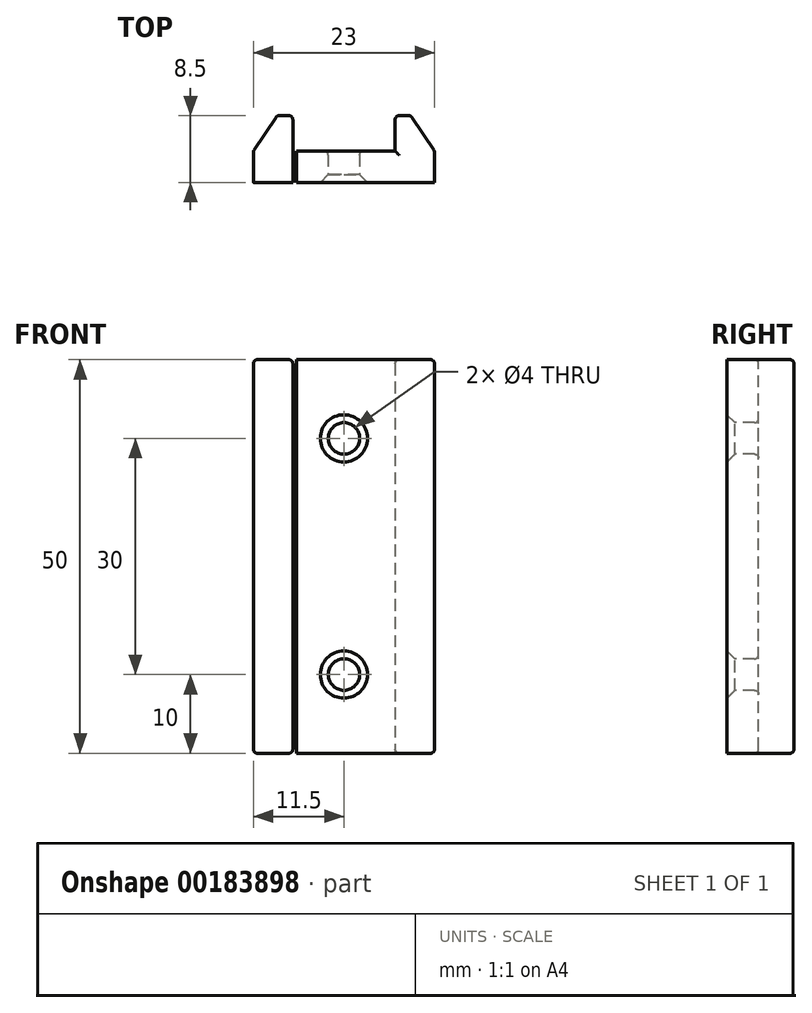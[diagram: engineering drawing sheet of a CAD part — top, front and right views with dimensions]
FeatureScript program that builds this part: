
annotation { "Feature Type Name" : "Feature", "Feature Type Description" : "" }
export const myFeature = defineFeature(function(context is Context, id is Id, definition is map)
    precondition{}
    {
        {
            var Q0;
            Q0=qCreatedBy(makeId("Front.planeOp"),FACE);
            var sketch = newSketch(context, id + "F0", { "sketchPlane" : qUnion([Q0])});
            skLineSegment(sketch, "E0.bottom", {"start": v(6, -25) * mm, "end": v(-6, -25) * mm});
            skLineSegment(sketch, "E0.top", {"start": v(6, 25) * mm, "end": v(-6, 25) * mm});
            skLineSegment(sketch, "E0.left", {"start": v(6, -25) * mm, "end": v(6, 25) * mm});
            skLineSegment(sketch, "E0.right", {"start": v(-6, -25) * mm, "end": v(-6, 25) * mm});
            skPoint(sketch, "E0.middle", {"position": v(0, 0) * mm});
            skLineSegment(sketch, "E1.bottom", {"start": v(-6, 25) * mm, "end": v(-11.5, 25) * mm});
            skLineSegment(sketch, "E1.top", {"start": v(-6, -25) * mm, "end": v(-11.5, -25) * mm});
            skLineSegment(sketch, "E1.left", {"start": v(-6, 25) * mm, "end": v(-6, -25) * mm});
            skLineSegment(sketch, "E1.right", {"start": v(-11.5, 25) * mm, "end": v(-11.5, -25) * mm});
            skLineSegment(sketch, "E2.MirrorCS", {"start": v(6.5, 25) * mm, "end": v(11.5, 25) * mm});
            skLineSegment(sketch, "E3.MirrorCS", {"start": v(11.5, 25) * mm, "end": v(11.5, -25) * mm});
            skLineSegment(sketch, "E4.MirrorCS", {"start": v(6.5, -25) * mm, "end": v(11.5, -25) * mm});
            skLineSegment(sketch, "E5.0", {"start": v(-6.5, 25) * mm, "end": v(-6.5, -25) * mm});
            skLineSegment(sketch, "E6.MirrorCS", {"start": v(6.5, 25) * mm, "end": v(6.5, -25) * mm});
            skLineSegment(sketch, "E7", {"start": v(0, 25) * mm, "end": v(0, -25) * mm, "construction": true});
            skLineSegment(sketch, "E8", {"start": v(-11.5, -15) * mm, "end": v(11.5, -15) * mm, "construction": true});
            skLineSegment(sketch, "E9", {"start": v(-11.5, 15) * mm, "end": v(11.5, 15) * mm, "construction": true});
            skCircle(sketch, "E10", {"center": v(0, 15) * mm, "radius": 2 * mm});
            skCircle(sketch, "E11", {"center": v(0, -15) * mm, "radius": 2 * mm});
            skLineSegment(sketch, "E12", {"start": v(6.5, 25) * mm, "end": v(6, 25) * mm});
            skLineSegment(sketch, "E13", {"start": v(6.5, -25) * mm, "end": v(6, -25) * mm});
            skSolve(sketch);
        }
        {
            var Q0;
            Q0=makeQuery(id+"F0.imprint","IMPRINT",FACE,{"disambiguationData":[TD([[makeQuery(id+"F0.imprint","IMPRINT",EDGE,{"derivedFrom":sQuery(id+"F0.wireOp",EDGE,"E0.bottom")}),-1.0]])]});
            var Q1;
            {var subQ1=sQuery(id+"F0.wireOp",EDGE,"E1.right");Q1=makeQuery(id+"F0.imprint","IMPRINT",FACE,{"disambiguationData":[TD([[makeQuery(id+"F0.imprint","IMPRINT",EDGE,{"derivedFrom":subQ1}),1.0]])]});}
            var Q2;
            {var subQ0=sQuery(id+"F0.wireOp",EDGE,"E1.left");Q2=makeQuery(id+"F0.imprint","IMPRINT",FACE,{"disambiguationData":[TD([[makeQuery(id+"F0.imprint","IMPRINT",EDGE,{"derivedFrom":subQ0}),-1.0]])]});}
            var Q3;
            Q3=makeQuery(id+"F0.imprint","IMPRINT",FACE,{"disambiguationData":[TD([[makeQuery(id+"F0.imprint","IMPRINT",EDGE,{"derivedFrom":sQuery(id+"F0.wireOp",EDGE,"E0.left")}),-1.0]])]});
            var Q4;
            Q4=makeQuery(id+"F0.imprint","IMPRINT",FACE,{"disambiguationData":[TD([[makeQuery(id+"F0.imprint","IMPRINT",EDGE,{"derivedFrom":sQuery(id+"F0.wireOp",EDGE,"E2.MirrorCS")}),-1.0]])]});
            extrude(context, id + "F1", {"entities" : qUnion([Q0, Q1, Q2, Q3, Q4]), "oppositeDirection" : true, "depth" : 4 * mm});
        }
        {
            var Q0;
            {var subQ0=sQuery(id+"F0.wireOp",EDGE,"E1.right");Q0=makeQuery(id+"F0.imprint","IMPRINT",FACE,{"disambiguationData":[TD([[makeQuery(id+"F0.imprint","IMPRINT",EDGE,{"derivedFrom":subQ0}),1.0]])]});}
            var Q1;
            {var subQ0=sQuery(id+"F0.wireOp",EDGE,"E3.MirrorCS");Q1=makeQuery(id+"F0.imprint","IMPRINT",FACE,{"disambiguationData":[TD([[makeQuery(id+"F0.imprint","IMPRINT",EDGE,{"derivedFrom":subQ0}),-1.0]])]});}
            extrude(context, id + "F2", {"entities" : qUnion([Q0, Q1]), "operationType" : NewBodyOperationType.ADD, "oppositeDirection" : true, "depth" : 8.5 * mm});
        }
        {
            var Q0;
            Q0=makeQuery(id+"F2.opExtrude","CAP_EDGE",EDGE,{"disambiguationData":[OSD([sQuery(id+"F0.wireOp",EDGE,"E1.right")])],"isStart":false});
            chamfer(context, id + "F3", {"entities" : qUnion([Q0]), "chamferType" : ChamferType.TWO_OFFSETS, "width1" : 4.5 * mm, "oppositeDirection" : false, "width2" : 3 * mm});
        }
        {
            var Q0;
            Q0=makeQuery(id+"F2.opExtrude","CAP_EDGE",EDGE,{"disambiguationData":[OSD([sQuery(id+"F0.wireOp",EDGE,"E3.MirrorCS")])],"isStart":false});
            chamfer(context, id + "F4", {"entities" : qUnion([Q0]), "chamferType" : ChamferType.TWO_OFFSETS, "width1" : 4.5 * mm, "oppositeDirection" : true, "width2" : 3 * mm, "tangentPropagation" : true});
        }
        {
            var Q0;
            Q0=sQuery(id+"F0.wireOp",VERTEX,"E10.center");
            var Q1;
            Q1=sQuery(id+"F0.wireOp",VERTEX,"E11.center");
            var Q2;
            Q2=makeQuery(id+"F1.opExtrude","SWEPT_BODY",BODY,{"disambiguationData":[OSD([sQuery(id+"F0.wireOp",EDGE,"E0.bottom"),sQuery(id+"F0.wireOp",EDGE,"E0.top"),sQuery(id+"F0.wireOp",EDGE,"E1.bottom"),sQuery(id+"F0.wireOp",EDGE,"E1.top"),sQuery(id+"F0.wireOp",EDGE,"E1.right"),sQuery(id+"F0.wireOp",EDGE,"E2.MirrorCS"),sQuery(id+"F0.wireOp",EDGE,"E3.MirrorCS"),sQuery(id+"F0.wireOp",EDGE,"E4.MirrorCS"),sQuery(id+"F0.wireOp",EDGE,"E10"),sQuery(id+"F0.wireOp",EDGE,"E11"),sQuery(id+"F0.wireOp",EDGE,"E12"),sQuery(id+"F0.wireOp",EDGE,"E13")])]});
            hole(context, id + "F5", {"style" : HoleStyle.C_SINK, "endStyle" : HoleEndStyle.THROUGH, "holeDiameter" : 4 * mm, "cSinkDiameter" : 6 * mm, "cSinkAngle" : 90 * degree, "locations" : qUnion([Q0, Q1]), "scope" : qUnion([Q2]), "isTappedThrough" : true});
        }
        {
            var Q0;
            Q0=makeQuery(id+"Fde6kDLOxshh8E3_1.opExtrude","SWEPT_FACE",FACE,{"disambiguationData":[OSD([sQuery(id+"F0.wireOp",EDGE,"T33Nxz9f-G0tn-xnhC-FvTE-fY2xuErrY73N")])]});
            var Q1;
            Q1=makeQuery(id+"Fde6kDLOxshh8E3_1.opExtrude","SWEPT_FACE",FACE,{"disambiguationData":[OSD([sQuery(id+"F0.wireOp",EDGE,"da0ba401-8d94-4197-b795-813e0965d0f9")])]});
            var Q2;
            Q2=makeQuery(id+"Fde6kDLOxshh8E3_1.opExtrude","SWEPT_FACE",FACE,{"disambiguationData":[OSD([sQuery(id+"F0.wireOp",EDGE,"e77e1b9a-007d-4c83-9508-98feed9c690b")])]});
            var Q3;
            Q3=makeQuery(id+"Fde6kDLOxshh8E3_1.opExtrude","SWEPT_FACE",FACE,{"disambiguationData":[OSD([sQuery(id+"F0.wireOp",EDGE,"39f81b70-e8c2-4875-9376-20bc0b2a6c3b")])]});
            var Q4;
            Q4=makeQuery(id+"F4.opChamfer","BLEND_FACE",FACE,{"disambiguationData":[OSD([sQuery(id+"F0.wireOp",EDGE,"E3.MirrorCS")])]});
            var Q5;
            Q5=makeQuery(id+"F2.opExtrude","CAP_FACE",FACE,{"disambiguationData":[OSD([sQuery(id+"F0.wireOp",EDGE,"E2.MirrorCS"),sQuery(id+"F0.wireOp",EDGE,"E3.MirrorCS"),sQuery(id+"F0.wireOp",EDGE,"E4.MirrorCS"),sQuery(id+"F0.wireOp",EDGE,"E6.MirrorCS"),sQuery(id+"F0.wireOp",EDGE,"539f9750-dc91-464b-a573-112b15fa390c.0"),sQuery(id+"F0.wireOp",EDGE,"539f9750-dc91-464b-a573-112b15fa390c.1"),sQuery(id+"F0.wireOp",EDGE,"539f9750-dc91-464b-a573-112b15fa390c.2"),sQuery(id+"F0.wireOp",EDGE,"539f9750-dc91-464b-a573-112b15fa390c.3"),sQuery(id+"F0.wireOp",EDGE,"539f9750-dc91-464b-a573-112b15fa390c.4"),sQuery(id+"F0.wireOp",EDGE,"539f9750-dc91-464b-a573-112b15fa390c.5"),sQuery(id+"F0.wireOp",EDGE,"a8e38511-2c6b-4656-bbe2-a021e63cbe50.0"),sQuery(id+"F0.wireOp",EDGE,"a8e38511-2c6b-4656-bbe2-a021e63cbe50.1"),sQuery(id+"F0.wireOp",EDGE,"a8e38511-2c6b-4656-bbe2-a021e63cbe50.2"),sQuery(id+"F0.wireOp",EDGE,"a8e38511-2c6b-4656-bbe2-a021e63cbe50.3"),sQuery(id+"F0.wireOp",EDGE,"a8e38511-2c6b-4656-bbe2-a021e63cbe50.4"),sQuery(id+"F0.wireOp",EDGE,"a8e38511-2c6b-4656-bbe2-a021e63cbe50.5")])],"isStart":false});
            var Q6;
            Q6=makeQuery(id+"F2.opExtrude","CAP_FACE",FACE,{"disambiguationData":[OSD([sQuery(id+"F0.wireOp",EDGE,"E1.bottom"),sQuery(id+"F0.wireOp",EDGE,"E1.top"),sQuery(id+"F0.wireOp",EDGE,"E1.right"),sQuery(id+"F0.wireOp",EDGE,"E5.0"),sQuery(id+"F0.wireOp",EDGE,"23c44e91-364b-44a9-8542-abd9dcfbb523.0"),sQuery(id+"F0.wireOp",EDGE,"23c44e91-364b-44a9-8542-abd9dcfbb523.1"),sQuery(id+"F0.wireOp",EDGE,"23c44e91-364b-44a9-8542-abd9dcfbb523.2"),sQuery(id+"F0.wireOp",EDGE,"23c44e91-364b-44a9-8542-abd9dcfbb523.3"),sQuery(id+"F0.wireOp",EDGE,"23c44e91-364b-44a9-8542-abd9dcfbb523.4"),sQuery(id+"F0.wireOp",EDGE,"23c44e91-364b-44a9-8542-abd9dcfbb523.5"),sQuery(id+"F0.wireOp",EDGE,"c08f9198-67c1-4cca-93f6-4b56ce47e8c6.0"),sQuery(id+"F0.wireOp",EDGE,"c08f9198-67c1-4cca-93f6-4b56ce47e8c6.1"),sQuery(id+"F0.wireOp",EDGE,"c08f9198-67c1-4cca-93f6-4b56ce47e8c6.2"),sQuery(id+"F0.wireOp",EDGE,"c08f9198-67c1-4cca-93f6-4b56ce47e8c6.3"),sQuery(id+"F0.wireOp",EDGE,"c08f9198-67c1-4cca-93f6-4b56ce47e8c6.4"),sQuery(id+"F0.wireOp",EDGE,"c08f9198-67c1-4cca-93f6-4b56ce47e8c6.5")])],"isStart":false});
            var Q7;
            Q7=makeQuery(id+"F3.opChamfer","BLEND_FACE",FACE,{"disambiguationData":[OSD([sQuery(id+"F0.wireOp",EDGE,"E1.right")])]});
            var Q8;
            Q8=makeQuery(id+"F1.opExtrude","CAP_EDGE",EDGE,{"disambiguationData":[OSD([sQuery(id+"F0.wireOp",EDGE,"E11")])],"isStart":false});
            var Q9;
            Q9=makeQuery(id+"F1.opExtrude","CAP_EDGE",EDGE,{"disambiguationData":[OSD([sQuery(id+"F0.wireOp",EDGE,"E10")])],"isStart":false});
            var Q10;
            Q10=makeQuery(id+"F1.opExtrude","CAP_EDGE",EDGE,{"disambiguationData":[OSD([sQuery(id+"F0.wireOp",EDGE,"E0.bottom"),sQuery(id+"F0.wireOp",EDGE,"E1.top"),sQuery(id+"F0.wireOp",EDGE,"E4.MirrorCS"),sQuery(id+"F0.wireOp",EDGE,"E13")])],"isStart":false});
            var Q11;
            Q11=makeQuery(id+"F2.opExtrude","SWEPT_EDGE",EDGE,{"disambiguationData":[OSD([sQuery(id+"F0.wireOp",EDGE,"E4.MirrorCS"),sQuery(id+"F0.wireOp",EDGE,"E6.MirrorCS"),sQuery(id+"F0.wireOp",EDGE,"E13")])]});
            var Q12;
            Q12=makeQuery(id+"F2.opExtrude","SWEPT_EDGE",EDGE,{"disambiguationData":[OSD([sQuery(id+"F0.wireOp",EDGE,"E1.top"),sQuery(id+"F0.wireOp",EDGE,"E5.0")])]});
            var Q13;
            {var subQ0=sQuery(id+"F0.wireOp",EDGE,"E1.right");var subQ1=sQuery(id+"F0.wireOp",EDGE,"E1.top");Q13=makeQuery(id+"F2.boolean.opBoolean","MERGE",EDGE,{"derivedFrom":[makeQuery(id+"F1.opExtrude","SWEPT_EDGE",EDGE,{"disambiguationData":[OSD([subQ1,subQ0])]}),makeQuery(id+"F2.opExtrude","SWEPT_EDGE",EDGE,{"disambiguationData":[OSD([subQ1,subQ0])]})]});}
            var Q14;
            {var subQ0=sQuery(id+"F0.wireOp",EDGE,"E4.MirrorCS");var subQ1=sQuery(id+"F0.wireOp",EDGE,"E3.MirrorCS");Q14=makeQuery(id+"F2.boolean.opBoolean","MERGE",EDGE,{"derivedFrom":[makeQuery(id+"F1.opExtrude","SWEPT_EDGE",EDGE,{"disambiguationData":[OSD([subQ1,subQ0])]}),makeQuery(id+"F2.opExtrude","SWEPT_EDGE",EDGE,{"disambiguationData":[OSD([subQ1,subQ0])]})]});}
            var Q15;
            {var subQ0=sQuery(id+"F0.wireOp",EDGE,"E3.MirrorCS");var subQ1=sQuery(id+"F0.wireOp",EDGE,"E2.MirrorCS");Q15=makeQuery(id+"F2.boolean.opBoolean","MERGE",EDGE,{"derivedFrom":[makeQuery(id+"F1.opExtrude","SWEPT_EDGE",EDGE,{"disambiguationData":[OSD([subQ1,subQ0])]}),makeQuery(id+"F2.opExtrude","SWEPT_EDGE",EDGE,{"disambiguationData":[OSD([subQ1,subQ0])]})]});}
            var Q16;
            Q16=makeQuery(id+"F2.opExtrude","SWEPT_EDGE",EDGE,{"disambiguationData":[OSD([sQuery(id+"F0.wireOp",EDGE,"E2.MirrorCS"),sQuery(id+"F0.wireOp",EDGE,"E6.MirrorCS"),sQuery(id+"F0.wireOp",EDGE,"E12")])]});
            var Q17;
            Q17=makeQuery(id+"F1.opExtrude","CAP_EDGE",EDGE,{"disambiguationData":[OSD([sQuery(id+"F0.wireOp",EDGE,"E0.top"),sQuery(id+"F0.wireOp",EDGE,"E1.bottom"),sQuery(id+"F0.wireOp",EDGE,"E2.MirrorCS"),sQuery(id+"F0.wireOp",EDGE,"E12")])],"isStart":false});
            var Q18;
            Q18=makeQuery(id+"F2.opExtrude","SWEPT_EDGE",EDGE,{"disambiguationData":[OSD([sQuery(id+"F0.wireOp",EDGE,"E1.bottom"),sQuery(id+"F0.wireOp",EDGE,"E5.0")])]});
            var Q19;
            {var subQ0=sQuery(id+"F0.wireOp",EDGE,"E1.right");var subQ1=sQuery(id+"F0.wireOp",EDGE,"E1.bottom");Q19=makeQuery(id+"F2.boolean.opBoolean","MERGE",EDGE,{"derivedFrom":[makeQuery(id+"F1.opExtrude","SWEPT_EDGE",EDGE,{"disambiguationData":[OSD([subQ1,subQ0])]}),makeQuery(id+"F2.opExtrude","SWEPT_EDGE",EDGE,{"disambiguationData":[OSD([subQ1,subQ0])]})]});}
            fillet(context, id + "F6", {"entities" : qUnion([Q0, Q1, Q2, Q3, Q4, Q5, Q6, Q7, Q8, Q9, Q10, Q11, Q12, Q13, Q14, Q15, Q16, Q17, Q18, Q19]), "radius" : 0.5 * mm, "tangentPropagation" : true, "allowEdgeOverflow" : false});
        }
    });
